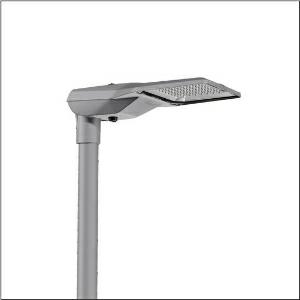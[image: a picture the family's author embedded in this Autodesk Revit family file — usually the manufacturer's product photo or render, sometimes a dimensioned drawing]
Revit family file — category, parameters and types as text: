
# Revit family: streetlight_sl_21_iq_midi___stw1_0a_5xe3e31y08nb_e460
name_source: partatom
category: Lighting Fixtures
units: mm (PartAtom-declared; Revit-internal decimal feet)

## family parameters
Cut with Voids When Loaded = No
Host = Face
Light Source = No
Part Type = Normal
Room Calculation Point = No
Round Connector Dimension = Use Diameter
Shared = No

## types (1)
- --- (1 x LED, 21550 lm, 136.6 W, 3000K)
    Apparent Load = 137 VA
    CIE Flux Codes = 39 75 98 100 100
    Color Rendering = 70
    Color Temperature = 3000K
    Default Elevation = 1800 mm
    Description = Streetlight SL 21 iQ midi, mast luminaire, primary light control with lens, of PMMA, primary optical cover: cover, of toughened safety glass, transparent, light distribution: STW1.0a, light emission: direct distribution, primary light characteristic: asymmetric, installation type: post-top, side-entry, LED, High Power LED, rated luminous flux: 21.550lm, luminous efficacy: 158lm/W, light colour: 730, colour temperature: 3000K, control gear: iQ-Street Remote, D4i with power reduction, control: pre-setting: logarithmic dimming characteristic, Street-Remote, Auto-Match, Temp-Guard, Lumen-Switch, Night-Set, Smart-Wire, Light-Fading, Desk-Remote (wireless, voltage-free reading and setting of iQ features in the workshop via application-optimized NFC function/RFID function), optimised constant luminous flux control (CLO 2.0), mains connection: 230..240V, AC, 50/60Hz, start of lifetime: 137W, end of service life: 144W, reduction: 61W, luminaire housing, of diecast aluminium, powder-coated, SITECO metallic grey (DB 702S), corrosivity category C5 high according to DIN EN ISO 12944, please order mast flange separately, inclination adjustable: 0°, 5°, 10°, 15°, sealing non-destructively replaceable, multi-level sealing system, length: 644mm, width: 335mm, height: 110mm, mast flange for spigot size: 42mm (side-entry): 5XC10008XM4, 60/48mm (side-entry/post-top): 5XC10108XM2, 76/60mm (side-entry/post-top): 5XC10108XM1, mounting height: 4..8m, Smart Interface below and above, protection rating (complete): IP66, insulation class (complete): insulation class II (safety insulation), certification: CE, ENEC, ENEC+, VDE, impact resistance: IK10, permissible operating ambient temperature for outdoor applications: -40..+50°C, standard-compliant lighting for roads and squares, packaging unit: 1 piece

Light Distribution: STW1.0a
    Height = 111 mm
    Lamp = 1 x LED
    Lamp Light Flux = 21550 lm
    Lamp Power = 136.6 W
    Lamp count = 1
    Length = 644 mm
    Luminous efficacy = 158 lm/W
    Manufacturer = Siteco
    ModVariant = No
    Model = 5XE3E31Y08NB
    Number of Poles = 1
    OnlyDefault = Yes
    Power Factor = 1
    Product Name = Streetlight SL 21 iQ midi | STW1.0a
    Product group = mast luminaire | pylon top
    ProductGroupID = 6100
    Protection Class = Protection class II
    Protection Degree = IP 66
    RLX_Detail_Level = 1
    RLX_Emergency_Light_Flux = 0 lm
    RLX_Emergency_Type = 0
    RLX_Emergency_Type_DB = No
    RlxData = <blob elided: 91309 chars, md5=141b4438>
    Socket = socket
    Standby Power = 0 W
    System Light Flux = 21550 lm
    System Power = 137 W
    Type Comments = factory setting: luminous flux: 100 % | dim-lin: 254 | 733 mA
    Type Image = l_1004304.jpg
    URL = http://relux.com
    VarID = @adj_113777
    Voltage = 0 V
    Weight = 0.00 kg
    Width = 336 mm

## geometry (parser evidence)
native form markers: Blend x4, Sweep x11
no freeform markers — native parametric forms only
